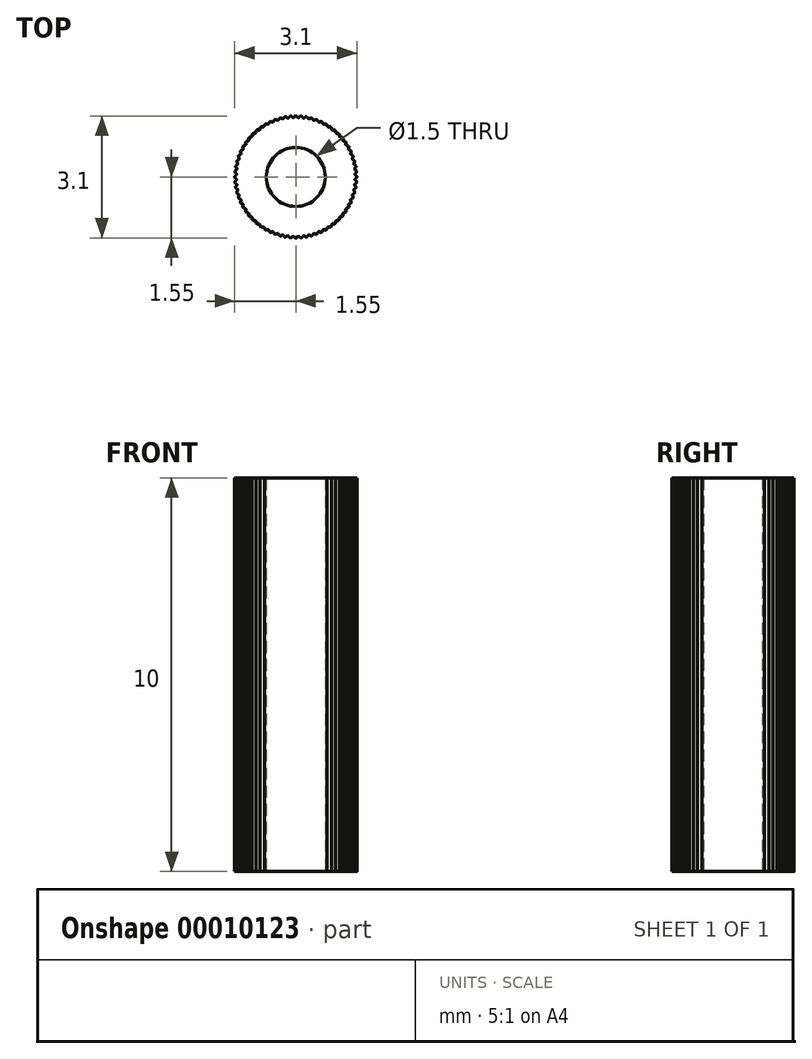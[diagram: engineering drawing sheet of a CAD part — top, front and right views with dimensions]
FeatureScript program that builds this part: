
annotation { "Feature Type Name" : "Feature", "Feature Type Description" : "" }
export const myFeature = defineFeature(function(context is Context, id is Id, definition is map)
    precondition{}
    {
        {
            var Q0;
            Q0=qCreatedBy(makeId("Top.planeOp"),FACE);
            var sketch = newSketch(context, id + "F0", { "sketchPlane" : qUnion([Q0])});
            skCircle(sketch, "E0", {"center": v(0, 0) * mm, "radius": 0.75 * mm});
            skCircle(sketch, "E1", {"center": v(0, 0) * mm, "radius": 1.55 * mm, "construction": true});
            skLineSegment(sketch, "E2", {"start": v(0, 0) * mm, "end": v(0, 1.55) * mm, "construction": true});
            skLineSegment(sketch, "E3", {"start": v(0, 0) * mm, "end": v(0.14, 1.54) * mm, "construction": true});
            skArc(sketch, "E4", {"start": v(0.03, 1.53) * mm, "mid": v(0.02, 1.54) * mm, "end": v(0, 1.55) * mm});
            skArc(sketch, "E5", {"start": v(0.03, 1.53) * mm, "mid": v(0.07, 1.51) * mm, "end": v(0.1, 1.53) * mm});
            skArc(sketch, "E6", {"start": v(0.14, 1.54) * mm, "mid": v(0.12, 1.54) * mm, "end": v(0.1, 1.53) * mm});
            skCircle(sketch, "E7", {"center": v(0, 0) * mm, "radius": 1.51 * mm, "construction": true});
            skArc(sketch, "E8.1.0", {"start": v(-0.1, 1.53) * mm, "mid": v(-0.12, 1.54) * mm, "end": v(-0.14, 1.54) * mm});
            skArc(sketch, "E8.1.1", {"start": v(-0.1, 1.53) * mm, "mid": v(-0.07, 1.51) * mm, "end": v(-0.03, 1.53) * mm});
            skArc(sketch, "E8.1.2", {"start": v(0, 1.55) * mm, "mid": v(-0.02, 1.54) * mm, "end": v(-0.03, 1.53) * mm});
            skArc(sketch, "E8.2.0", {"start": v(-0.23, 1.51) * mm, "mid": v(-0.25, 1.52) * mm, "end": v(-0.27, 1.53) * mm});
            skArc(sketch, "E8.2.1", {"start": v(-0.23, 1.51) * mm, "mid": v(-0.2, 1.5) * mm, "end": v(-0.17, 1.52) * mm});
            skArc(sketch, "E8.2.2", {"start": v(-0.14, 1.54) * mm, "mid": v(-0.15, 1.54) * mm, "end": v(-0.17, 1.52) * mm});
            skArc(sketch, "E8.3.0", {"start": v(-0.36, 1.49) * mm, "mid": v(-0.38, 1.5) * mm, "end": v(-0.4, 1.5) * mm});
            skArc(sketch, "E8.3.1", {"start": v(-0.36, 1.49) * mm, "mid": v(-0.33, 1.48) * mm, "end": v(-0.3, 1.5) * mm});
            skArc(sketch, "E8.3.2", {"start": v(-0.27, 1.53) * mm, "mid": v(-0.29, 1.52) * mm, "end": v(-0.3, 1.5) * mm});
            skArc(sketch, "E8.4.0", {"start": v(-0.5, 1.45) * mm, "mid": v(-0.5, 1.46) * mm, "end": v(-0.53, 1.46) * mm});
            skArc(sketch, "E8.4.1", {"start": v(-0.5, 1.45) * mm, "mid": v(-0.45, 1.44) * mm, "end": v(-0.43, 1.47) * mm});
            skArc(sketch, "E8.4.2", {"start": v(-0.4, 1.5) * mm, "mid": v(-0.42, 1.49) * mm, "end": v(-0.43, 1.47) * mm});
            skArc(sketch, "E8.5.0", {"start": v(-0.62, 1.4) * mm, "mid": v(-0.63, 1.4) * mm, "end": v(-0.66, 1.4) * mm});
            skArc(sketch, "E8.5.1", {"start": v(-0.62, 1.4) * mm, "mid": v(-0.58, 1.4) * mm, "end": v(-0.56, 1.43) * mm});
            skArc(sketch, "E8.5.2", {"start": v(-0.53, 1.46) * mm, "mid": v(-0.55, 1.44) * mm, "end": v(-0.56, 1.43) * mm});
            skArc(sketch, "E8.6.0", {"start": v(-0.74, 1.34) * mm, "mid": v(-0.76, 1.35) * mm, "end": v(-0.78, 1.34) * mm});
            skArc(sketch, "E8.6.1", {"start": v(-0.74, 1.34) * mm, "mid": v(-0.7, 1.34) * mm, "end": v(-0.68, 1.37) * mm});
            skArc(sketch, "E8.6.2", {"start": v(-0.66, 1.4) * mm, "mid": v(-0.67, 1.4) * mm, "end": v(-0.68, 1.37) * mm});
            skArc(sketch, "E8.7.0", {"start": v(-0.85, 1.27) * mm, "mid": v(-0.87, 1.28) * mm, "end": v(-0.89, 1.27) * mm});
            skArc(sketch, "E8.7.1", {"start": v(-0.85, 1.27) * mm, "mid": v(-0.81, 1.27) * mm, "end": v(-0.8, 1.3) * mm});
            skArc(sketch, "E8.7.2", {"start": v(-0.78, 1.34) * mm, "mid": v(-0.79, 1.33) * mm, "end": v(-0.8, 1.3) * mm});
            skArc(sketch, "E8.8.0", {"start": v(-0.96, 1.2) * mm, "mid": v(-0.98, 1.2) * mm, "end": v(-1, 1.19) * mm});
            skArc(sketch, "E8.8.1", {"start": v(-0.96, 1.2) * mm, "mid": v(-0.92, 1.2) * mm, "end": v(-0.9, 1.23) * mm});
            skArc(sketch, "E8.8.2", {"start": v(-0.89, 1.27) * mm, "mid": v(-0.9, 1.25) * mm, "end": v(-0.9, 1.23) * mm});
            skArc(sketch, "E8.9.0", {"start": v(-1.06, 1.1) * mm, "mid": v(-1.08, 1.1) * mm, "end": v(-1.1, 1.1) * mm});
            skArc(sketch, "E8.9.1", {"start": v(-1.06, 1.1) * mm, "mid": v(-1.02, 1.11) * mm, "end": v(-1, 1.15) * mm});
            skArc(sketch, "E8.9.2", {"start": v(-1, 1.19) * mm, "mid": v(-1, 1.17) * mm, "end": v(-1, 1.15) * mm});
            skArc(sketch, "E8.10.0", {"start": v(-1.15, 1) * mm, "mid": v(-1.17, 1) * mm, "end": v(-1.19, 1) * mm});
            skArc(sketch, "E8.10.1", {"start": v(-1.15, 1) * mm, "mid": v(-1.11, 1.02) * mm, "end": v(-1.1, 1.06) * mm});
            skArc(sketch, "E8.10.2", {"start": v(-1.1, 1.1) * mm, "mid": v(-1.1, 1.08) * mm, "end": v(-1.1, 1.06) * mm});
            skArc(sketch, "E8.11.0", {"start": v(-1.23, 0.9) * mm, "mid": v(-1.25, 0.9) * mm, "end": v(-1.27, 0.89) * mm});
            skArc(sketch, "E8.11.1", {"start": v(-1.23, 0.9) * mm, "mid": v(-1.2, 0.92) * mm, "end": v(-1.2, 0.96) * mm});
            skArc(sketch, "E8.11.2", {"start": v(-1.19, 1) * mm, "mid": v(-1.2, 0.98) * mm, "end": v(-1.2, 0.96) * mm});
            skArc(sketch, "E8.12.0", {"start": v(-1.3, 0.8) * mm, "mid": v(-1.33, 0.79) * mm, "end": v(-1.34, 0.78) * mm});
            skArc(sketch, "E8.12.1", {"start": v(-1.3, 0.8) * mm, "mid": v(-1.27, 0.81) * mm, "end": v(-1.27, 0.85) * mm});
            skArc(sketch, "E8.12.2", {"start": v(-1.27, 0.89) * mm, "mid": v(-1.28, 0.87) * mm, "end": v(-1.27, 0.85) * mm});
            skArc(sketch, "E8.13.0", {"start": v(-1.37, 0.68) * mm, "mid": v(-1.4, 0.67) * mm, "end": v(-1.4, 0.66) * mm});
            skArc(sketch, "E8.13.1", {"start": v(-1.37, 0.68) * mm, "mid": v(-1.34, 0.7) * mm, "end": v(-1.34, 0.74) * mm});
            skArc(sketch, "E8.13.2", {"start": v(-1.34, 0.77) * mm, "mid": v(-1.35, 0.76) * mm, "end": v(-1.34, 0.74) * mm});
            skArc(sketch, "E8.14.0", {"start": v(-1.43, 0.56) * mm, "mid": v(-1.44, 0.55) * mm, "end": v(-1.46, 0.53) * mm});
            skArc(sketch, "E8.14.1", {"start": v(-1.43, 0.56) * mm, "mid": v(-1.4, 0.58) * mm, "end": v(-1.4, 0.62) * mm});
            skArc(sketch, "E8.14.2", {"start": v(-1.4, 0.66) * mm, "mid": v(-1.4, 0.63) * mm, "end": v(-1.4, 0.62) * mm});
            skArc(sketch, "E8.15.0", {"start": v(-1.47, 0.43) * mm, "mid": v(-1.49, 0.42) * mm, "end": v(-1.5, 0.4) * mm});
            skArc(sketch, "E8.15.1", {"start": v(-1.47, 0.43) * mm, "mid": v(-1.44, 0.45) * mm, "end": v(-1.45, 0.5) * mm});
            skArc(sketch, "E8.15.2", {"start": v(-1.46, 0.53) * mm, "mid": v(-1.46, 0.5) * mm, "end": v(-1.45, 0.5) * mm});
            skArc(sketch, "E8.16.0", {"start": v(-1.5, 0.3) * mm, "mid": v(-1.52, 0.29) * mm, "end": v(-1.53, 0.27) * mm});
            skArc(sketch, "E8.16.1", {"start": v(-1.5, 0.3) * mm, "mid": v(-1.48, 0.33) * mm, "end": v(-1.49, 0.36) * mm});
            skArc(sketch, "E8.16.2", {"start": v(-1.5, 0.4) * mm, "mid": v(-1.5, 0.38) * mm, "end": v(-1.49, 0.36) * mm});
            skArc(sketch, "E8.17.0", {"start": v(-1.52, 0.17) * mm, "mid": v(-1.54, 0.15) * mm, "end": v(-1.54, 0.14) * mm});
            skArc(sketch, "E8.17.1", {"start": v(-1.52, 0.17) * mm, "mid": v(-1.5, 0.2) * mm, "end": v(-1.51, 0.23) * mm});
            skArc(sketch, "E8.17.2", {"start": v(-1.53, 0.27) * mm, "mid": v(-1.52, 0.25) * mm, "end": v(-1.51, 0.23) * mm});
            skArc(sketch, "E8.18.0", {"start": v(-1.53, 0.03) * mm, "mid": v(-1.54, 0.02) * mm, "end": v(-1.55, 0) * mm});
            skArc(sketch, "E8.18.1", {"start": v(-1.53, 0.03) * mm, "mid": v(-1.51, 0.07) * mm, "end": v(-1.53, 0.1) * mm});
            skArc(sketch, "E8.18.2", {"start": v(-1.54, 0.14) * mm, "mid": v(-1.54, 0.12) * mm, "end": v(-1.53, 0.1) * mm});
            skArc(sketch, "E8.19.0", {"start": v(-1.53, -0.1) * mm, "mid": v(-1.54, -0.12) * mm, "end": v(-1.54, -0.14) * mm});
            skArc(sketch, "E8.19.1", {"start": v(-1.53, -0.1) * mm, "mid": v(-1.51, -0.07) * mm, "end": v(-1.53, -0.03) * mm});
            skArc(sketch, "E8.19.2", {"start": v(-1.55, 0) * mm, "mid": v(-1.54, -0.02) * mm, "end": v(-1.53, -0.03) * mm});
            skArc(sketch, "E8.20.0", {"start": v(-1.51, -0.23) * mm, "mid": v(-1.52, -0.25) * mm, "end": v(-1.53, -0.27) * mm});
            skArc(sketch, "E8.20.1", {"start": v(-1.51, -0.23) * mm, "mid": v(-1.5, -0.2) * mm, "end": v(-1.52, -0.17) * mm});
            skArc(sketch, "E8.20.2", {"start": v(-1.54, -0.14) * mm, "mid": v(-1.54, -0.15) * mm, "end": v(-1.52, -0.17) * mm});
            skArc(sketch, "E8.21.0", {"start": v(-1.49, -0.36) * mm, "mid": v(-1.5, -0.38) * mm, "end": v(-1.5, -0.4) * mm});
            skArc(sketch, "E8.21.1", {"start": v(-1.49, -0.36) * mm, "mid": v(-1.48, -0.33) * mm, "end": v(-1.5, -0.3) * mm});
            skArc(sketch, "E8.21.2", {"start": v(-1.53, -0.27) * mm, "mid": v(-1.52, -0.29) * mm, "end": v(-1.5, -0.3) * mm});
            skArc(sketch, "E8.22.0", {"start": v(-1.45, -0.5) * mm, "mid": v(-1.46, -0.5) * mm, "end": v(-1.46, -0.53) * mm});
            skArc(sketch, "E8.22.1", {"start": v(-1.45, -0.5) * mm, "mid": v(-1.44, -0.45) * mm, "end": v(-1.47, -0.43) * mm});
            skArc(sketch, "E8.22.2", {"start": v(-1.5, -0.4) * mm, "mid": v(-1.49, -0.42) * mm, "end": v(-1.47, -0.43) * mm});
            skArc(sketch, "E8.23.0", {"start": v(-1.4, -0.62) * mm, "mid": v(-1.4, -0.63) * mm, "end": v(-1.4, -0.66) * mm});
            skArc(sketch, "E8.23.1", {"start": v(-1.4, -0.62) * mm, "mid": v(-1.4, -0.58) * mm, "end": v(-1.43, -0.56) * mm});
            skArc(sketch, "E8.23.2", {"start": v(-1.46, -0.53) * mm, "mid": v(-1.44, -0.55) * mm, "end": v(-1.43, -0.56) * mm});
            skArc(sketch, "E8.24.0", {"start": v(-1.34, -0.74) * mm, "mid": v(-1.35, -0.76) * mm, "end": v(-1.34, -0.77) * mm});
            skArc(sketch, "E8.24.1", {"start": v(-1.34, -0.74) * mm, "mid": v(-1.34, -0.7) * mm, "end": v(-1.37, -0.68) * mm});
            skArc(sketch, "E8.24.2", {"start": v(-1.4, -0.66) * mm, "mid": v(-1.4, -0.67) * mm, "end": v(-1.37, -0.68) * mm});
            skArc(sketch, "E8.25.0", {"start": v(-1.27, -0.85) * mm, "mid": v(-1.28, -0.87) * mm, "end": v(-1.27, -0.89) * mm});
            skArc(sketch, "E8.25.1", {"start": v(-1.27, -0.85) * mm, "mid": v(-1.27, -0.81) * mm, "end": v(-1.3, -0.8) * mm});
            skArc(sketch, "E8.25.2", {"start": v(-1.34, -0.78) * mm, "mid": v(-1.33, -0.79) * mm, "end": v(-1.3, -0.8) * mm});
            skArc(sketch, "E8.26.0", {"start": v(-1.2, -0.96) * mm, "mid": v(-1.2, -0.98) * mm, "end": v(-1.19, -1) * mm});
            skArc(sketch, "E8.26.1", {"start": v(-1.2, -0.96) * mm, "mid": v(-1.2, -0.92) * mm, "end": v(-1.23, -0.9) * mm});
            skArc(sketch, "E8.26.2", {"start": v(-1.27, -0.89) * mm, "mid": v(-1.25, -0.9) * mm, "end": v(-1.23, -0.9) * mm});
            skArc(sketch, "E8.27.0", {"start": v(-1.1, -1.06) * mm, "mid": v(-1.1, -1.08) * mm, "end": v(-1.1, -1.1) * mm});
            skArc(sketch, "E8.27.1", {"start": v(-1.1, -1.06) * mm, "mid": v(-1.11, -1.02) * mm, "end": v(-1.15, -1) * mm});
            skArc(sketch, "E8.27.2", {"start": v(-1.19, -1) * mm, "mid": v(-1.17, -1) * mm, "end": v(-1.15, -1) * mm});
            skArc(sketch, "E8.28.0", {"start": v(-1, -1.15) * mm, "mid": v(-1, -1.17) * mm, "end": v(-1, -1.19) * mm});
            skArc(sketch, "E8.28.1", {"start": v(-1, -1.15) * mm, "mid": v(-1.02, -1.11) * mm, "end": v(-1.06, -1.1) * mm});
            skArc(sketch, "E8.28.2", {"start": v(-1.1, -1.1) * mm, "mid": v(-1.08, -1.1) * mm, "end": v(-1.06, -1.1) * mm});
            skArc(sketch, "E8.29.0", {"start": v(-0.9, -1.23) * mm, "mid": v(-0.9, -1.25) * mm, "end": v(-0.89, -1.27) * mm});
            skArc(sketch, "E8.29.1", {"start": v(-0.9, -1.23) * mm, "mid": v(-0.92, -1.2) * mm, "end": v(-0.96, -1.2) * mm});
            skArc(sketch, "E8.29.2", {"start": v(-1, -1.19) * mm, "mid": v(-0.98, -1.2) * mm, "end": v(-0.96, -1.2) * mm});
            skArc(sketch, "E8.30.0", {"start": v(-0.8, -1.3) * mm, "mid": v(-0.79, -1.33) * mm, "end": v(-0.77, -1.34) * mm});
            skArc(sketch, "E8.30.1", {"start": v(-0.8, -1.3) * mm, "mid": v(-0.81, -1.27) * mm, "end": v(-0.85, -1.27) * mm});
            skArc(sketch, "E8.30.2", {"start": v(-0.89, -1.27) * mm, "mid": v(-0.87, -1.28) * mm, "end": v(-0.85, -1.27) * mm});
            skArc(sketch, "E8.31.0", {"start": v(-0.68, -1.37) * mm, "mid": v(-0.67, -1.4) * mm, "end": v(-0.66, -1.4) * mm});
            skArc(sketch, "E8.31.1", {"start": v(-0.68, -1.37) * mm, "mid": v(-0.7, -1.34) * mm, "end": v(-0.74, -1.34) * mm});
            skArc(sketch, "E8.31.2", {"start": v(-0.77, -1.34) * mm, "mid": v(-0.76, -1.35) * mm, "end": v(-0.74, -1.34) * mm});
            skArc(sketch, "E8.32.0", {"start": v(-0.56, -1.43) * mm, "mid": v(-0.55, -1.44) * mm, "end": v(-0.53, -1.46) * mm});
            skArc(sketch, "E8.32.1", {"start": v(-0.56, -1.43) * mm, "mid": v(-0.58, -1.4) * mm, "end": v(-0.62, -1.4) * mm});
            skArc(sketch, "E8.32.2", {"start": v(-0.66, -1.4) * mm, "mid": v(-0.63, -1.4) * mm, "end": v(-0.62, -1.4) * mm});
            skArc(sketch, "E8.33.0", {"start": v(-0.43, -1.47) * mm, "mid": v(-0.42, -1.49) * mm, "end": v(-0.4, -1.5) * mm});
            skArc(sketch, "E8.33.1", {"start": v(-0.43, -1.47) * mm, "mid": v(-0.45, -1.44) * mm, "end": v(-0.5, -1.45) * mm});
            skArc(sketch, "E8.33.2", {"start": v(-0.53, -1.46) * mm, "mid": v(-0.5, -1.46) * mm, "end": v(-0.5, -1.45) * mm});
            skArc(sketch, "E8.34.0", {"start": v(-0.3, -1.5) * mm, "mid": v(-0.29, -1.52) * mm, "end": v(-0.27, -1.53) * mm});
            skArc(sketch, "E8.34.1", {"start": v(-0.3, -1.5) * mm, "mid": v(-0.33, -1.48) * mm, "end": v(-0.36, -1.49) * mm});
            skArc(sketch, "E8.34.2", {"start": v(-0.4, -1.5) * mm, "mid": v(-0.38, -1.5) * mm, "end": v(-0.36, -1.49) * mm});
            skArc(sketch, "E8.35.0", {"start": v(-0.17, -1.52) * mm, "mid": v(-0.15, -1.54) * mm, "end": v(-0.14, -1.54) * mm});
            skArc(sketch, "E8.35.1", {"start": v(-0.17, -1.52) * mm, "mid": v(-0.2, -1.5) * mm, "end": v(-0.23, -1.51) * mm});
            skArc(sketch, "E8.35.2", {"start": v(-0.27, -1.53) * mm, "mid": v(-0.25, -1.52) * mm, "end": v(-0.23, -1.51) * mm});
            skArc(sketch, "E8.36.0", {"start": v(-0.03, -1.53) * mm, "mid": v(-0.02, -1.54) * mm, "end": v(0, -1.55) * mm});
            skArc(sketch, "E8.36.1", {"start": v(-0.03, -1.53) * mm, "mid": v(-0.07, -1.51) * mm, "end": v(-0.1, -1.53) * mm});
            skArc(sketch, "E8.36.2", {"start": v(-0.14, -1.54) * mm, "mid": v(-0.12, -1.54) * mm, "end": v(-0.1, -1.53) * mm});
            skArc(sketch, "E8.37.0", {"start": v(0.1, -1.53) * mm, "mid": v(0.12, -1.54) * mm, "end": v(0.14, -1.54) * mm});
            skArc(sketch, "E8.37.1", {"start": v(0.1, -1.53) * mm, "mid": v(0.07, -1.51) * mm, "end": v(0.03, -1.53) * mm});
            skArc(sketch, "E8.37.2", {"start": v(0, -1.55) * mm, "mid": v(0.02, -1.54) * mm, "end": v(0.03, -1.53) * mm});
            skArc(sketch, "E8.38.0", {"start": v(0.23, -1.51) * mm, "mid": v(0.25, -1.52) * mm, "end": v(0.27, -1.53) * mm});
            skArc(sketch, "E8.38.1", {"start": v(0.23, -1.51) * mm, "mid": v(0.2, -1.5) * mm, "end": v(0.17, -1.52) * mm});
            skArc(sketch, "E8.38.2", {"start": v(0.14, -1.54) * mm, "mid": v(0.15, -1.54) * mm, "end": v(0.17, -1.52) * mm});
            skArc(sketch, "E8.39.0", {"start": v(0.36, -1.49) * mm, "mid": v(0.38, -1.5) * mm, "end": v(0.4, -1.5) * mm});
            skArc(sketch, "E8.39.1", {"start": v(0.36, -1.49) * mm, "mid": v(0.33, -1.48) * mm, "end": v(0.3, -1.5) * mm});
            skArc(sketch, "E8.39.2", {"start": v(0.27, -1.53) * mm, "mid": v(0.29, -1.52) * mm, "end": v(0.3, -1.5) * mm});
            skArc(sketch, "E8.40.0", {"start": v(0.5, -1.45) * mm, "mid": v(0.5, -1.46) * mm, "end": v(0.53, -1.46) * mm});
            skArc(sketch, "E8.40.1", {"start": v(0.5, -1.45) * mm, "mid": v(0.45, -1.44) * mm, "end": v(0.43, -1.47) * mm});
            skArc(sketch, "E8.40.2", {"start": v(0.4, -1.5) * mm, "mid": v(0.42, -1.49) * mm, "end": v(0.43, -1.47) * mm});
            skArc(sketch, "E8.41.0", {"start": v(0.62, -1.4) * mm, "mid": v(0.63, -1.4) * mm, "end": v(0.66, -1.4) * mm});
            skArc(sketch, "E8.41.1", {"start": v(0.62, -1.4) * mm, "mid": v(0.58, -1.4) * mm, "end": v(0.56, -1.43) * mm});
            skArc(sketch, "E8.41.2", {"start": v(0.53, -1.46) * mm, "mid": v(0.55, -1.44) * mm, "end": v(0.56, -1.43) * mm});
            skArc(sketch, "E8.42.0", {"start": v(0.74, -1.34) * mm, "mid": v(0.76, -1.35) * mm, "end": v(0.77, -1.34) * mm});
            skArc(sketch, "E8.42.1", {"start": v(0.74, -1.34) * mm, "mid": v(0.7, -1.34) * mm, "end": v(0.68, -1.37) * mm});
            skArc(sketch, "E8.42.2", {"start": v(0.66, -1.4) * mm, "mid": v(0.67, -1.4) * mm, "end": v(0.68, -1.37) * mm});
            skArc(sketch, "E8.43.0", {"start": v(0.85, -1.27) * mm, "mid": v(0.87, -1.28) * mm, "end": v(0.89, -1.27) * mm});
            skArc(sketch, "E8.43.1", {"start": v(0.85, -1.27) * mm, "mid": v(0.81, -1.27) * mm, "end": v(0.8, -1.3) * mm});
            skArc(sketch, "E8.43.2", {"start": v(0.78, -1.34) * mm, "mid": v(0.79, -1.33) * mm, "end": v(0.8, -1.3) * mm});
            skArc(sketch, "E8.44.0", {"start": v(0.96, -1.2) * mm, "mid": v(0.98, -1.2) * mm, "end": v(1, -1.19) * mm});
            skArc(sketch, "E8.44.1", {"start": v(0.96, -1.2) * mm, "mid": v(0.92, -1.2) * mm, "end": v(0.9, -1.23) * mm});
            skArc(sketch, "E8.44.2", {"start": v(0.89, -1.27) * mm, "mid": v(0.9, -1.25) * mm, "end": v(0.9, -1.23) * mm});
            skArc(sketch, "E8.45.0", {"start": v(1.06, -1.1) * mm, "mid": v(1.08, -1.1) * mm, "end": v(1.1, -1.1) * mm});
            skArc(sketch, "E8.45.1", {"start": v(1.06, -1.1) * mm, "mid": v(1.02, -1.11) * mm, "end": v(1, -1.15) * mm});
            skArc(sketch, "E8.45.2", {"start": v(1, -1.19) * mm, "mid": v(1, -1.17) * mm, "end": v(1, -1.15) * mm});
            skArc(sketch, "E8.46.0", {"start": v(1.15, -1) * mm, "mid": v(1.17, -1) * mm, "end": v(1.19, -1) * mm});
            skArc(sketch, "E8.46.1", {"start": v(1.15, -1) * mm, "mid": v(1.11, -1.02) * mm, "end": v(1.1, -1.06) * mm});
            skArc(sketch, "E8.46.2", {"start": v(1.1, -1.1) * mm, "mid": v(1.1, -1.08) * mm, "end": v(1.1, -1.06) * mm});
            skArc(sketch, "E8.47.0", {"start": v(1.23, -0.9) * mm, "mid": v(1.25, -0.9) * mm, "end": v(1.27, -0.89) * mm});
            skArc(sketch, "E8.47.1", {"start": v(1.23, -0.9) * mm, "mid": v(1.2, -0.92) * mm, "end": v(1.2, -0.96) * mm});
            skArc(sketch, "E8.47.2", {"start": v(1.19, -1) * mm, "mid": v(1.2, -0.98) * mm, "end": v(1.2, -0.96) * mm});
            skArc(sketch, "E8.48.0", {"start": v(1.3, -0.8) * mm, "mid": v(1.33, -0.79) * mm, "end": v(1.34, -0.78) * mm});
            skArc(sketch, "E8.48.1", {"start": v(1.3, -0.8) * mm, "mid": v(1.27, -0.81) * mm, "end": v(1.27, -0.85) * mm});
            skArc(sketch, "E8.48.2", {"start": v(1.27, -0.89) * mm, "mid": v(1.28, -0.87) * mm, "end": v(1.27, -0.85) * mm});
            skArc(sketch, "E8.49.0", {"start": v(1.37, -0.68) * mm, "mid": v(1.4, -0.67) * mm, "end": v(1.4, -0.66) * mm});
            skArc(sketch, "E8.49.1", {"start": v(1.37, -0.68) * mm, "mid": v(1.34, -0.7) * mm, "end": v(1.34, -0.74) * mm});
            skArc(sketch, "E8.49.2", {"start": v(1.34, -0.78) * mm, "mid": v(1.35, -0.76) * mm, "end": v(1.34, -0.74) * mm});
            skArc(sketch, "E8.50.0", {"start": v(1.43, -0.56) * mm, "mid": v(1.44, -0.55) * mm, "end": v(1.46, -0.53) * mm});
            skArc(sketch, "E8.50.1", {"start": v(1.43, -0.56) * mm, "mid": v(1.4, -0.58) * mm, "end": v(1.4, -0.62) * mm});
            skArc(sketch, "E8.50.2", {"start": v(1.4, -0.66) * mm, "mid": v(1.4, -0.63) * mm, "end": v(1.4, -0.62) * mm});
            skArc(sketch, "E8.51.0", {"start": v(1.47, -0.43) * mm, "mid": v(1.49, -0.42) * mm, "end": v(1.5, -0.4) * mm});
            skArc(sketch, "E8.51.1", {"start": v(1.47, -0.43) * mm, "mid": v(1.44, -0.45) * mm, "end": v(1.45, -0.5) * mm});
            skArc(sketch, "E8.51.2", {"start": v(1.46, -0.53) * mm, "mid": v(1.46, -0.5) * mm, "end": v(1.45, -0.5) * mm});
            skArc(sketch, "E8.52.0", {"start": v(1.5, -0.3) * mm, "mid": v(1.52, -0.29) * mm, "end": v(1.53, -0.27) * mm});
            skArc(sketch, "E8.52.1", {"start": v(1.5, -0.3) * mm, "mid": v(1.48, -0.33) * mm, "end": v(1.49, -0.36) * mm});
            skArc(sketch, "E8.52.2", {"start": v(1.5, -0.4) * mm, "mid": v(1.5, -0.38) * mm, "end": v(1.49, -0.36) * mm});
            skArc(sketch, "E8.53.0", {"start": v(1.52, -0.17) * mm, "mid": v(1.54, -0.15) * mm, "end": v(1.54, -0.14) * mm});
            skArc(sketch, "E8.53.1", {"start": v(1.52, -0.17) * mm, "mid": v(1.5, -0.2) * mm, "end": v(1.51, -0.23) * mm});
            skArc(sketch, "E8.53.2", {"start": v(1.53, -0.27) * mm, "mid": v(1.52, -0.25) * mm, "end": v(1.51, -0.23) * mm});
            skArc(sketch, "E8.54.0", {"start": v(1.53, -0.03) * mm, "mid": v(1.54, -0.02) * mm, "end": v(1.55, 0) * mm});
            skArc(sketch, "E8.54.1", {"start": v(1.53, -0.03) * mm, "mid": v(1.51, -0.07) * mm, "end": v(1.53, -0.1) * mm});
            skArc(sketch, "E8.54.2", {"start": v(1.54, -0.14) * mm, "mid": v(1.54, -0.12) * mm, "end": v(1.53, -0.1) * mm});
            skArc(sketch, "E8.55.0", {"start": v(1.53, 0.1) * mm, "mid": v(1.54, 0.12) * mm, "end": v(1.54, 0.14) * mm});
            skArc(sketch, "E8.55.1", {"start": v(1.53, 0.1) * mm, "mid": v(1.51, 0.07) * mm, "end": v(1.53, 0.03) * mm});
            skArc(sketch, "E8.55.2", {"start": v(1.55, 0) * mm, "mid": v(1.54, 0.02) * mm, "end": v(1.53, 0.03) * mm});
            skArc(sketch, "E8.56.0", {"start": v(1.51, 0.23) * mm, "mid": v(1.52, 0.25) * mm, "end": v(1.53, 0.27) * mm});
            skArc(sketch, "E8.56.1", {"start": v(1.51, 0.23) * mm, "mid": v(1.5, 0.2) * mm, "end": v(1.52, 0.17) * mm});
            skArc(sketch, "E8.56.2", {"start": v(1.54, 0.14) * mm, "mid": v(1.54, 0.15) * mm, "end": v(1.52, 0.17) * mm});
            skArc(sketch, "E8.57.0", {"start": v(1.49, 0.36) * mm, "mid": v(1.5, 0.38) * mm, "end": v(1.5, 0.4) * mm});
            skArc(sketch, "E8.57.1", {"start": v(1.49, 0.36) * mm, "mid": v(1.48, 0.33) * mm, "end": v(1.5, 0.3) * mm});
            skArc(sketch, "E8.57.2", {"start": v(1.53, 0.27) * mm, "mid": v(1.52, 0.29) * mm, "end": v(1.5, 0.3) * mm});
            skArc(sketch, "E8.58.0", {"start": v(1.45, 0.5) * mm, "mid": v(1.46, 0.5) * mm, "end": v(1.46, 0.53) * mm});
            skArc(sketch, "E8.58.1", {"start": v(1.45, 0.5) * mm, "mid": v(1.44, 0.45) * mm, "end": v(1.47, 0.43) * mm});
            skArc(sketch, "E8.58.2", {"start": v(1.5, 0.4) * mm, "mid": v(1.49, 0.42) * mm, "end": v(1.47, 0.43) * mm});
            skArc(sketch, "E8.59.0", {"start": v(1.4, 0.62) * mm, "mid": v(1.4, 0.63) * mm, "end": v(1.4, 0.66) * mm});
            skArc(sketch, "E8.59.1", {"start": v(1.4, 0.62) * mm, "mid": v(1.4, 0.58) * mm, "end": v(1.43, 0.56) * mm});
            skArc(sketch, "E8.59.2", {"start": v(1.46, 0.53) * mm, "mid": v(1.44, 0.55) * mm, "end": v(1.43, 0.56) * mm});
            skArc(sketch, "E8.60.0", {"start": v(1.34, 0.74) * mm, "mid": v(1.35, 0.76) * mm, "end": v(1.34, 0.78) * mm});
            skArc(sketch, "E8.60.1", {"start": v(1.34, 0.74) * mm, "mid": v(1.34, 0.7) * mm, "end": v(1.37, 0.68) * mm});
            skArc(sketch, "E8.60.2", {"start": v(1.4, 0.66) * mm, "mid": v(1.4, 0.67) * mm, "end": v(1.37, 0.68) * mm});
            skArc(sketch, "E8.61.0", {"start": v(1.27, 0.85) * mm, "mid": v(1.28, 0.87) * mm, "end": v(1.27, 0.89) * mm});
            skArc(sketch, "E8.61.1", {"start": v(1.27, 0.85) * mm, "mid": v(1.27, 0.81) * mm, "end": v(1.3, 0.8) * mm});
            skArc(sketch, "E8.61.2", {"start": v(1.34, 0.78) * mm, "mid": v(1.33, 0.79) * mm, "end": v(1.3, 0.8) * mm});
            skArc(sketch, "E8.62.0", {"start": v(1.2, 0.96) * mm, "mid": v(1.2, 0.98) * mm, "end": v(1.19, 1) * mm});
            skArc(sketch, "E8.62.1", {"start": v(1.2, 0.96) * mm, "mid": v(1.2, 0.92) * mm, "end": v(1.23, 0.9) * mm});
            skArc(sketch, "E8.62.2", {"start": v(1.27, 0.89) * mm, "mid": v(1.25, 0.9) * mm, "end": v(1.23, 0.9) * mm});
            skArc(sketch, "E8.63.0", {"start": v(1.1, 1.06) * mm, "mid": v(1.1, 1.08) * mm, "end": v(1.1, 1.1) * mm});
            skArc(sketch, "E8.63.1", {"start": v(1.1, 1.06) * mm, "mid": v(1.11, 1.02) * mm, "end": v(1.15, 1) * mm});
            skArc(sketch, "E8.63.2", {"start": v(1.19, 1) * mm, "mid": v(1.17, 1) * mm, "end": v(1.15, 1) * mm});
            skArc(sketch, "E8.64.0", {"start": v(1, 1.15) * mm, "mid": v(1, 1.17) * mm, "end": v(1, 1.19) * mm});
            skArc(sketch, "E8.64.1", {"start": v(1, 1.15) * mm, "mid": v(1.02, 1.11) * mm, "end": v(1.06, 1.1) * mm});
            skArc(sketch, "E8.64.2", {"start": v(1.1, 1.1) * mm, "mid": v(1.08, 1.1) * mm, "end": v(1.06, 1.1) * mm});
            skArc(sketch, "E8.65.0", {"start": v(0.9, 1.23) * mm, "mid": v(0.9, 1.25) * mm, "end": v(0.89, 1.27) * mm});
            skArc(sketch, "E8.65.1", {"start": v(0.9, 1.23) * mm, "mid": v(0.92, 1.2) * mm, "end": v(0.96, 1.2) * mm});
            skArc(sketch, "E8.65.2", {"start": v(1, 1.19) * mm, "mid": v(0.98, 1.2) * mm, "end": v(0.96, 1.2) * mm});
            skArc(sketch, "E8.66.0", {"start": v(0.8, 1.3) * mm, "mid": v(0.79, 1.33) * mm, "end": v(0.78, 1.34) * mm});
            skArc(sketch, "E8.66.1", {"start": v(0.8, 1.3) * mm, "mid": v(0.81, 1.27) * mm, "end": v(0.85, 1.27) * mm});
            skArc(sketch, "E8.66.2", {"start": v(0.89, 1.27) * mm, "mid": v(0.87, 1.28) * mm, "end": v(0.85, 1.27) * mm});
            skArc(sketch, "E8.67.0", {"start": v(0.68, 1.37) * mm, "mid": v(0.67, 1.4) * mm, "end": v(0.66, 1.4) * mm});
            skArc(sketch, "E8.67.1", {"start": v(0.68, 1.37) * mm, "mid": v(0.7, 1.34) * mm, "end": v(0.74, 1.34) * mm});
            skArc(sketch, "E8.67.2", {"start": v(0.78, 1.34) * mm, "mid": v(0.76, 1.35) * mm, "end": v(0.74, 1.34) * mm});
            skArc(sketch, "E8.68.0", {"start": v(0.56, 1.43) * mm, "mid": v(0.55, 1.44) * mm, "end": v(0.53, 1.46) * mm});
            skArc(sketch, "E8.68.1", {"start": v(0.56, 1.43) * mm, "mid": v(0.58, 1.4) * mm, "end": v(0.62, 1.4) * mm});
            skArc(sketch, "E8.68.2", {"start": v(0.66, 1.4) * mm, "mid": v(0.63, 1.4) * mm, "end": v(0.62, 1.4) * mm});
            skArc(sketch, "E8.69.0", {"start": v(0.43, 1.47) * mm, "mid": v(0.42, 1.49) * mm, "end": v(0.4, 1.5) * mm});
            skArc(sketch, "E8.69.1", {"start": v(0.43, 1.47) * mm, "mid": v(0.45, 1.44) * mm, "end": v(0.5, 1.45) * mm});
            skArc(sketch, "E8.69.2", {"start": v(0.53, 1.46) * mm, "mid": v(0.5, 1.46) * mm, "end": v(0.5, 1.45) * mm});
            skArc(sketch, "E8.70.0", {"start": v(0.3, 1.5) * mm, "mid": v(0.29, 1.52) * mm, "end": v(0.27, 1.53) * mm});
            skArc(sketch, "E8.70.1", {"start": v(0.3, 1.5) * mm, "mid": v(0.33, 1.48) * mm, "end": v(0.36, 1.49) * mm});
            skArc(sketch, "E8.70.2", {"start": v(0.4, 1.5) * mm, "mid": v(0.38, 1.5) * mm, "end": v(0.36, 1.49) * mm});
            skArc(sketch, "E8.71.0", {"start": v(0.17, 1.52) * mm, "mid": v(0.15, 1.54) * mm, "end": v(0.14, 1.54) * mm});
            skArc(sketch, "E8.71.1", {"start": v(0.17, 1.52) * mm, "mid": v(0.2, 1.5) * mm, "end": v(0.23, 1.51) * mm});
            skArc(sketch, "E8.71.2", {"start": v(0.27, 1.53) * mm, "mid": v(0.25, 1.52) * mm, "end": v(0.23, 1.51) * mm});
            skSolve(sketch);
        }
        {
            var Q0;
            Q0 = qSketchRegion(id + "F0", true);
            extrude(context, id + "F1", {"entities" : qUnion([Q0]), "depth" : 10 * mm});
        }
    });
